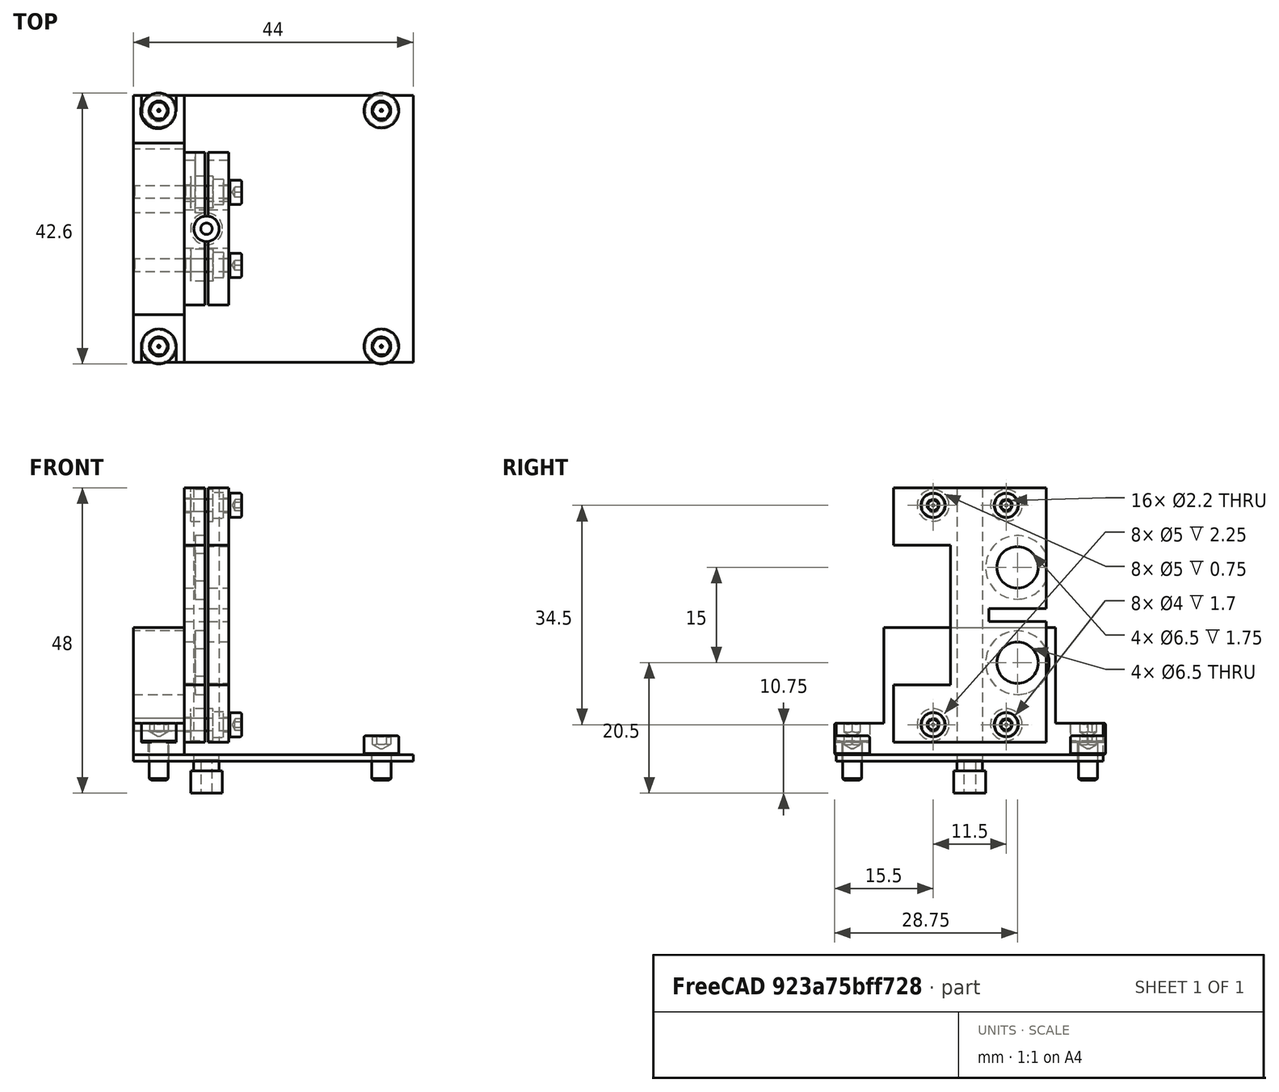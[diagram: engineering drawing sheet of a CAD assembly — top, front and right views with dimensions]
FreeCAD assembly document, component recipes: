
FREECAD ASSEMBLY — COMPONENT RECIPES ("Quak_XL30_Modulator2")

This assembly document has 16 components, labeled P0..P15 below (a component is one placed body or linked part). 0 of them carry a construction recipe — the FreeCAD feature program that regenerates the part from scratch, quoted from this document or its linked companion documents; the rest are supplied as boundary geometry only. No exploded tour is included for this assembly.
COMPONENT P0 — geometry summary ("Markor4mmOD_M2"; no construction recipe available for this part):
  bounding box: 5.2 x 5.0 x 5.0 mm
  tessellated surface: 1,764 triangles
  volume: 77 mm^3 (59% of its bounding box)
  symmetry: revolution-symmetric about the x axis through its bounding-box center; mirror-symmetric across its y mid-plane, z mid-plane
COMPONENT P1 — geometry summary ("Markor4mmOD_M003"; no construction recipe available for this part):
  bounding box: 5.2 x 5.0 x 5.0 mm
  tessellated surface: 1,764 triangles
  volume: 77 mm^3 (59% of its bounding box)
  symmetry: revolution-symmetric about the x axis through its bounding-box center; mirror-symmetric across its y mid-plane, z mid-plane
COMPONENT P2 — geometry summary ("Markor4mmOD_M004"; no construction recipe available for this part):
  bounding box: 5.2 x 5.0 x 5.0 mm
  tessellated surface: 1,764 triangles
  volume: 77 mm^3 (59% of its bounding box)
  symmetry: revolution-symmetric about the x axis through its bounding-box center; mirror-symmetric across its y mid-plane, z mid-plane
COMPONENT P3 — geometry summary ("Markor4mmOD_M005"; no construction recipe available for this part):
  bounding box: 5.2 x 5.0 x 5.0 mm
  tessellated surface: 1,764 triangles
  volume: 77 mm^3 (59% of its bounding box)
  symmetry: revolution-symmetric about the x axis through its bounding-box center; mirror-symmetric across its y mid-plane, z mid-plane
COMPONENT P4 — geometry summary ("Markor4mmOD_M006"; no construction recipe available for this part):
  bounding box: 5.2 x 5.0 x 5.0 mm
  tessellated surface: 1,764 triangles
  volume: 77 mm^3 (59% of its bounding box)
  symmetry: revolution-symmetric about the x axis through its bounding-box center; mirror-symmetric across its y mid-plane, z mid-plane
COMPONENT P5 — geometry summary ("Markor4mmOD_M007"; no construction recipe available for this part):
  bounding box: 5.2 x 5.0 x 5.0 mm
  tessellated surface: 1,764 triangles
  volume: 77 mm^3 (59% of its bounding box)
  symmetry: revolution-symmetric about the x axis through its bounding-box center; mirror-symmetric across its y mid-plane, z mid-plane
COMPONENT P6 — geometry summary ("Markor4mmOD_M008"; no construction recipe available for this part):
  bounding box: 5.2 x 5.0 x 5.0 mm
  tessellated surface: 1,764 triangles
  volume: 77 mm^3 (59% of its bounding box)
  symmetry: revolution-symmetric about the x axis through its bounding-box center; mirror-symmetric across its y mid-plane, z mid-plane
COMPONENT P7 — geometry summary ("Markor4mmOD_M009"; no construction recipe available for this part):
  bounding box: 5.2 x 5.0 x 5.0 mm
  tessellated surface: 1,764 triangles
  volume: 77 mm^3 (59% of its bounding box)
  symmetry: revolution-symmetric about the x axis through its bounding-box center; mirror-symmetric across its y mid-plane, z mid-plane
COMPONENT P8 — geometry summary ("Markor4mmOD_M012"; no construction recipe available for this part):
  bounding box: 5.2 x 5.0 x 5.0 mm
  tessellated surface: 1,764 triangles
  volume: 77 mm^3 (59% of its bounding box)
  symmetry: revolution-symmetric about the x axis through its bounding-box center; mirror-symmetric across its y mid-plane, z mid-plane
COMPONENT P9 — geometry summary ("Markor4mmOD_M013"; no construction recipe available for this part):
  bounding box: 5.2 x 5.0 x 5.0 mm
  tessellated surface: 1,764 triangles
  volume: 77 mm^3 (59% of its bounding box)
  symmetry: revolution-symmetric about the x axis through its bounding-box center; mirror-symmetric across its y mid-plane, z mid-plane
COMPONENT P10 — geometry summary ("Markor4mmOD_M014"; no construction recipe available for this part):
  bounding box: 5.2 x 5.0 x 5.0 mm
  tessellated surface: 1,764 triangles
  volume: 77 mm^3 (59% of its bounding box)
  symmetry: revolution-symmetric about the x axis through its bounding-box center; mirror-symmetric across its y mid-plane, z mid-plane
COMPONENT P11 — geometry summary ("Markor4mmOD_M015"; no construction recipe available for this part):
  bounding box: 5.2 x 5.0 x 5.0 mm
  tessellated surface: 1,764 triangles
  volume: 77 mm^3 (59% of its bounding box)
  symmetry: revolution-symmetric about the x axis through its bounding-box center; mirror-symmetric across its y mid-plane, z mid-plane
COMPONENT P12 — geometry summary ("Markor4mmOD_M016"; no construction recipe available for this part):
  bounding box: 5.2 x 5.0 x 5.0 mm
  tessellated surface: 1,764 triangles
  volume: 77 mm^3 (59% of its bounding box)
  symmetry: revolution-symmetric about the x axis through its bounding-box center; mirror-symmetric across its y mid-plane, z mid-plane
COMPONENT P13 — geometry summary ("Markor4mmOD_M017"; no construction recipe available for this part):
  bounding box: 5.2 x 5.0 x 5.0 mm
  tessellated surface: 1,764 triangles
  volume: 77 mm^3 (59% of its bounding box)
  symmetry: revolution-symmetric about the x axis through its bounding-box center; mirror-symmetric across its y mid-plane, z mid-plane
COMPONENT P14 — geometry summary ("Markor4mmOD_M018"; no construction recipe available for this part):
  bounding box: 5.2 x 5.0 x 5.0 mm
  tessellated surface: 1,764 triangles
  volume: 77 mm^3 (59% of its bounding box)
  symmetry: revolution-symmetric about the x axis through its bounding-box center; mirror-symmetric across its y mid-plane, z mid-plane
COMPONENT P15 — geometry summary ("Markor4mmOD_M019"; no construction recipe available for this part):
  bounding box: 5.2 x 5.0 x 5.0 mm
  tessellated surface: 1,764 triangles
  volume: 77 mm^3 (59% of its bounding box)
  symmetry: revolution-symmetric about the x axis through its bounding-box center; mirror-symmetric across its y mid-plane, z mid-plane
PROVENANCE & LICENSES
A FreeCAD (.FCStd) document from a public repository crawl; recipes are the document's own serialized feature recipes (and, for linked parts, companion documents' recipes).
License: bsd.
